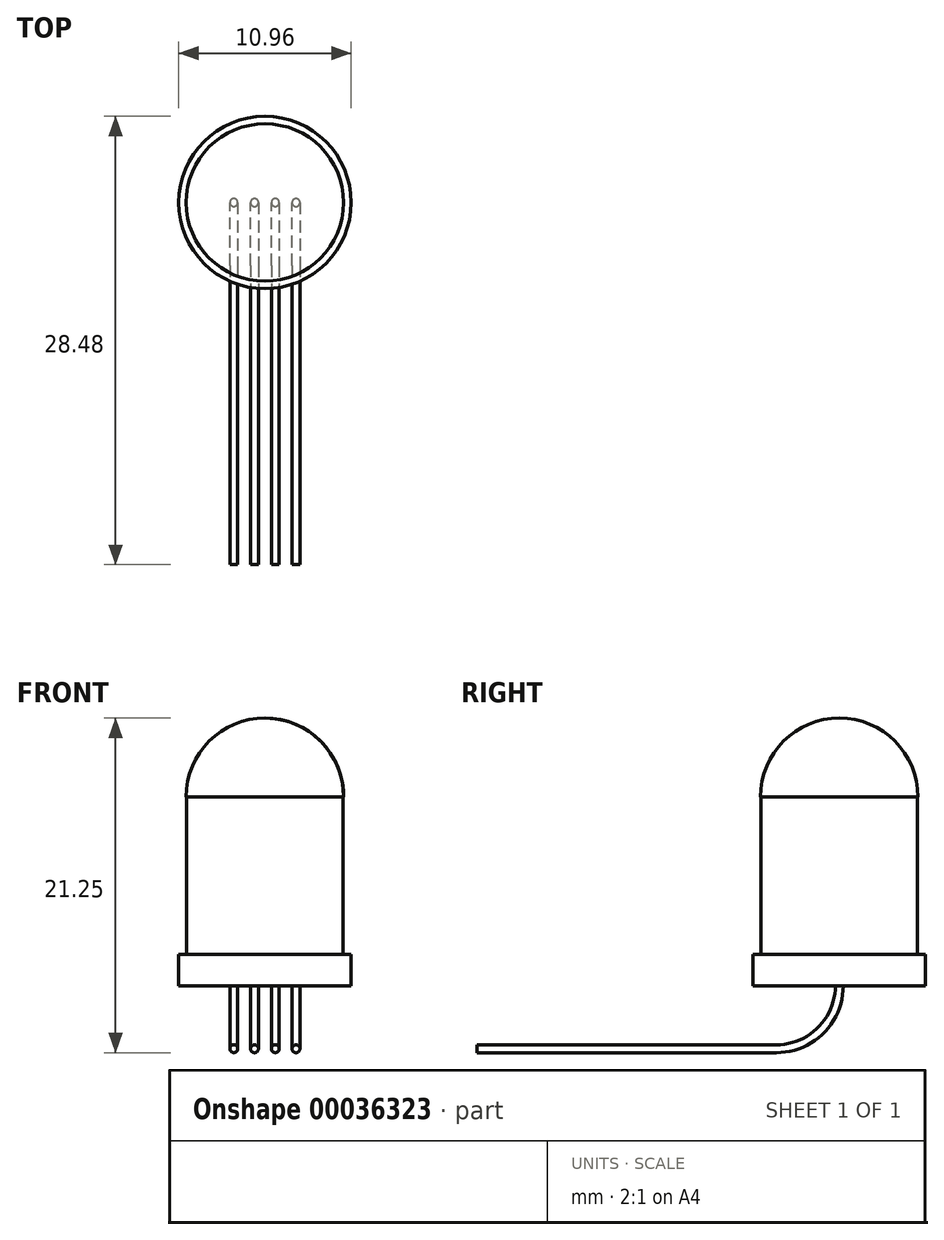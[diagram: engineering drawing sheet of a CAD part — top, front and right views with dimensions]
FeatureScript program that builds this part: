
annotation { "Feature Type Name" : "Feature", "Feature Type Description" : "" }
export const myFeature = defineFeature(function(context is Context, id is Id, definition is map)
    precondition{}
    {
        {
            var Q0;
            Q0=qCreatedBy(makeId("Top.planeOp"),FACE);
            var sketch = newSketch(context, id + "F0", { "sketchPlane" : qUnion([Q0])});
            skCircle(sketch, "E0", {"center": v(0, 0) * mm, "radius": 5.47 * mm});
            skSolve(sketch);
        }
        {
            var Q0;
            Q0 = qSketchRegion(id + "F0", true);
            extrude(context, id + "F1", {"entities" : qUnion([Q0]), "depth" : 2 * mm});
        }
        {
            var Q0;
            Q0=makeQuery(id+"F1.opExtrude","CAP_FACE",FACE,{"disambiguationData":[OSD([sQuery(id+"F0.wireOp",EDGE,"E0")])],"isStart":false});
            var sketch = newSketch(context, id + "F2", { "sketchPlane" : qUnion([Q0])});
            skCircle(sketch, "E1", {"center": v(0, 0) * mm, "radius": 4.97 * mm});
            skSolve(sketch);
        }
        {
            var Q0;
            Q0 = qSketchRegion(id + "F2", true);
            extrude(context, id + "F3", {"entities" : qUnion([Q0]), "operationType" : NewBodyOperationType.ADD, "depth" : 10 * mm});
        }
        {
            var Q0;
            Q0=qCreatedBy(makeId("Front.planeOp"),FACE);
            var sketch = newSketch(context, id + "F4", { "sketchPlane" : qUnion([Q0])});
            skLineSegment(sketch, "E2", {"start": v(0, 12) * mm, "end": v(5, 12) * mm});
            skLineSegment(sketch, "E3", {"start": v(0, 12) * mm, "end": v(0, 17) * mm});
            skArc(sketch, "E4", {"start": v(5, 12) * mm, "mid": v(3.54, 15.54) * mm, "end": v(0, 17) * mm});
            skSolve(sketch);
        }
        {
            var Q0;
            Q0=makeQuery(id+"F4.imprint","IMPRINT",FACE,{"disambiguationData":[TD([[makeQuery(id+"F4.imprint","IMPRINT",EDGE,{"derivedFrom":sQuery(id+"F4.wireOp",EDGE,"E2")}),1.0]])]});
            var Q1;
            Q1=sQuery(id+"F4.wireOp",EDGE,"E3");
            revolve(context, id + "F5", {"operationType" : NewBodyOperationType.ADD, "entities" : qUnion([Q0]), "axis" : qUnion([Q1]), "revolveType" : RevolveType.FULL});
        }
        {
            var Q0;
            Q0=qCreatedBy(makeId("Top.planeOp"),FACE);
            var sketch = newSketch(context, id + "F6", { "sketchPlane" : qUnion([Q0])});
            skCircle(sketch, "E5", {"center": v(-1.97, 0) * mm, "radius": 0.25 * mm});
            skCircle(sketch, "E6", {"center": v(1.97, 0) * mm, "radius": 0.25 * mm});
            skCircle(sketch, "E7", {"center": v(-0.66, 0) * mm, "radius": 0.25 * mm});
            skCircle(sketch, "E8", {"center": v(0.66, 0) * mm, "radius": 0.25 * mm});
            skSolve(sketch);
        }
        {
            var Q0;
            Q0=qCreatedBy(makeId("Right.planeOp"),FACE);
            cPlane(context, id + "F7", {"entities" : qUnion([Q0]), "cplaneType" : CPlaneType.OFFSET, "offset" : 1.97 * mm, "width" : 150 * mm, "height" : 150 * mm});
        }
        {
            var Q0;
            Q0=qCreatedBy(id+"F7.planeOp",FACE);
            var sketch = newSketch(context, id + "F8", { "sketchPlane" : qUnion([Q0])});
            skLineSegment(sketch, "E9", {"start": v(-4, -4) * mm, "end": v(-23, -4) * mm});
            skPoint(sketch, "E10", {"position": v(-4, -4) * mm});
            skArc(sketch, "E11", {"start": v(-4, -4) * mm, "mid": v(-1.17, -2.83) * mm, "end": v(0, 0) * mm});
            skSolve(sketch);
        }
        {
            var Q0;
            Q0 = qSketchRegion(id + "F6", true);
            var Q1;
            Q1 = qConstructionFilter(qBodyType(qCreatedBy(id + "F8" ,EDGE), BodyType.WIRE), ConstructionObject.NO);
            sweep(context, id + "F9", {"operationType" : NewBodyOperationType.ADD, "profiles" : qUnion([Q0]), "path" : qUnion([Q1])});
        }
    });
